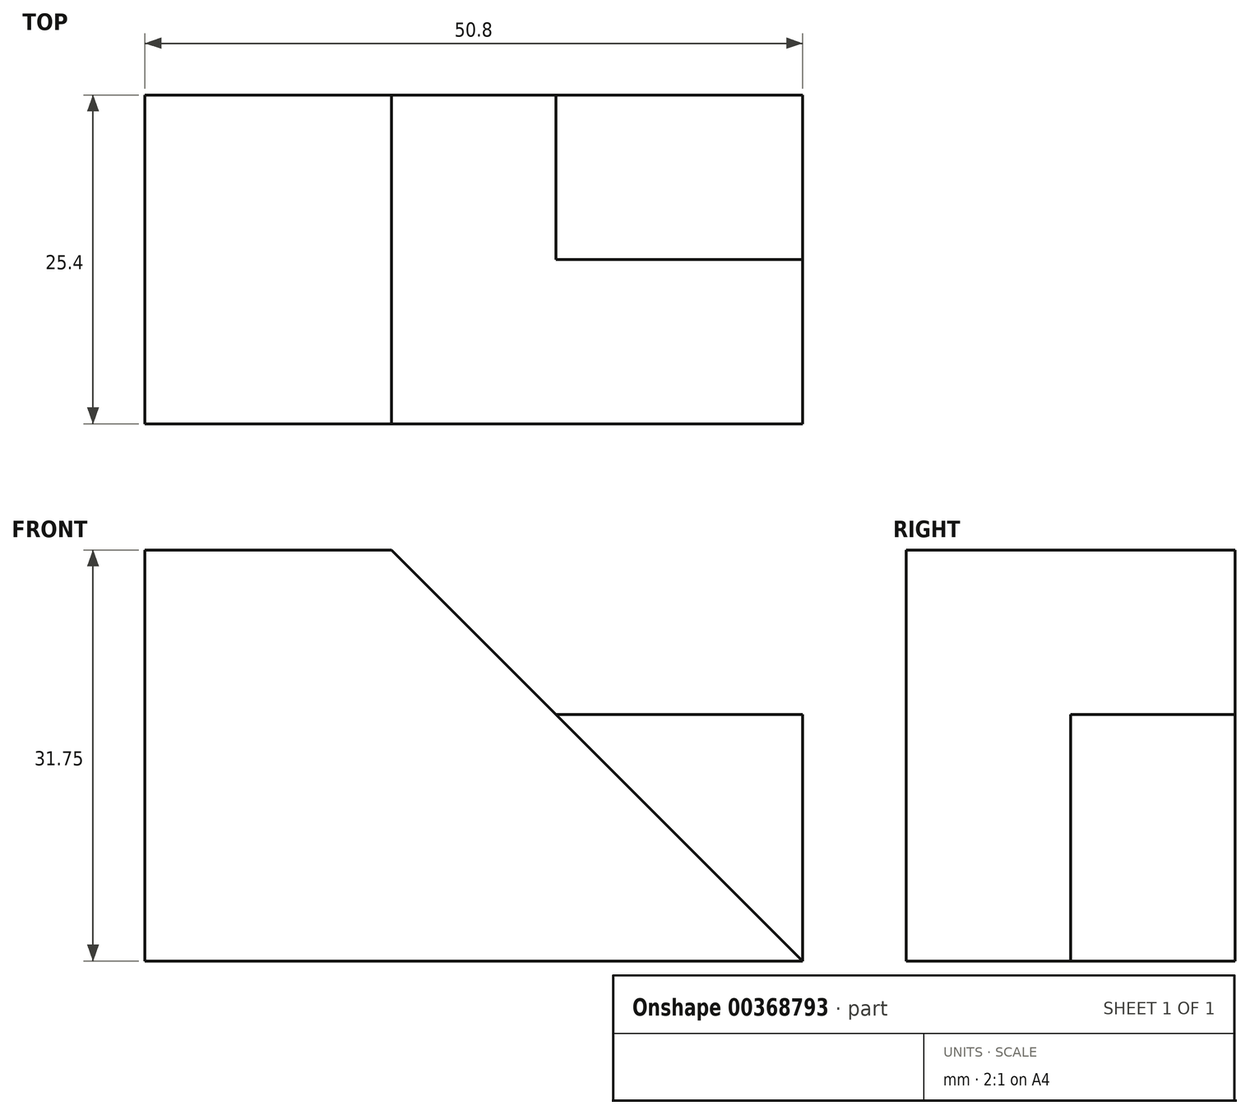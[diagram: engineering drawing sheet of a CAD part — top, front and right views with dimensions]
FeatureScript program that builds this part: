
annotation { "Feature Type Name" : "Feature", "Feature Type Description" : "" }
export const myFeature = defineFeature(function(context is Context, id is Id, definition is map)
    precondition{}
    {
        {
            var Q0;
            Q0=qCreatedBy(makeId("Front.planeOp"),FACE);
            var sketch = newSketch(context, id + "F0", { "sketchPlane" : qUnion([Q0])});
            skLineSegment(sketch, "E0.bottom", {"start": v(0, 31.75) * mm, "end": v(50.8, 31.75) * mm});
            skLineSegment(sketch, "E0.top", {"start": v(0, 0) * mm, "end": v(50.8, 0) * mm});
            skLineSegment(sketch, "E0.left", {"start": v(0, 31.75) * mm, "end": v(0, 0) * mm});
            skLineSegment(sketch, "E0.right", {"start": v(50.8, 31.75) * mm, "end": v(50.8, 0) * mm});
            skSolve(sketch);
        }
        {
            var Q0;
            Q0 = qSketchRegion(id + "FAowoq1lq1kOuDw_0", true);
            var Q1;
            Q1=makeQuery(id+"F0.imprint","IMPRINT",FACE,{"disambiguationData":[TD([[makeQuery(id+"F0.imprint","IMPRINT",EDGE,{"derivedFrom":sQuery(id+"F0.wireOp",EDGE,"E0.bottom")}),-1.0]])]});
            extrude(context, id + "F1", {"entities" : qUnion([Q0, Q1]), "depth" : 25.4 * mm});
        }
        {
            var Q0;
            Q0=makeQuery(id+"F1.opExtrude","CAP_FACE",FACE,{"disambiguationData":[OSD([sQuery(id+"F0.wireOp",EDGE,"E0.bottom"),sQuery(id+"F0.wireOp",EDGE,"E0.top"),sQuery(id+"F0.wireOp",EDGE,"E0.left"),sQuery(id+"F0.wireOp",EDGE,"E0.right")])],"isStart":false});
            var sketch = newSketch(context, id + "F2", { "sketchPlane" : qUnion([Q0])});
            skLineSegment(sketch, "E1", {"start": v(50.8, 0) * mm, "end": v(25.4, 31.75) * mm});
            skSolve(sketch);
        }
        {
            var Q0;
            {var subQ0=sQuery(id+"F2.wireOp",EDGE,"E1");Q0=makeQuery(id+"F2.imprint","IMPRINT",FACE,{"disambiguationData":[TD([[makeQuery(id+"F2.imprint","IMPRINT",EDGE,{"derivedFrom":subQ0}),-1.0]])]});}
            extrude(context, id + "F3", {"entities" : qUnion([Q0]), "operationType" : NewBodyOperationType.REMOVE, "oppositeDirection" : true, "depth" : 25.4 * mm});
        }
        {
            var Q0;
            Q0=makeQuery(id+"F3.boolean.opBoolean","COPY",FACE,{"derivedFrom":makeQuery(id+"F3.opExtrude","SWEPT_FACE",FACE,{"disambiguationData":[OSD([sQuery(id+"F2.wireOp",EDGE,"E1")])]})});
            extrude(context, id + "F4", {"entities" : qUnion([Q0]), "operationType" : NewBodyOperationType.ADD, "depth" : 25.4 * mm});
        }
        {
            var Q0;
            {var subQ0=sQuery(id+"F2.wireOp",EDGE,"E1");Q0=makeQuery(id+"F4.boolean.opBoolean","MERGE",FACE,{"derivedFrom":[makeQuery(id+"F1.opExtrude","CAP_FACE",FACE,{"disambiguationData":[OSD([sQuery(id+"F0.wireOp",EDGE,"E0.bottom"),sQuery(id+"F0.wireOp",EDGE,"E0.top"),sQuery(id+"F0.wireOp",EDGE,"E0.left"),sQuery(id+"F0.wireOp",EDGE,"E0.right")])],"isStart":false}),makeQuery(id+"F4.opExtrude","SWEPT_FACE",FACE,{"disambiguationData":[OSD([subQ0]),TDD([makeQuery(id+"F3.boolean.opBoolean","COPY",EDGE,{"derivedFrom":makeQuery(id+"F3.opExtrude","CAP_EDGE",EDGE,{"disambiguationData":[OSD([subQ0])],"isStart":true})})])]})]});}
            var sketch = newSketch(context, id + "F5", { "sketchPlane" : qUnion([Q0])});
            skLineSegment(sketch, "E2", {"start": v(25.4, 31.75) * mm, "end": v(50.8, 31.75) * mm});
            skLineSegment(sketch, "E3", {"start": v(50.8, 31.75) * mm, "end": v(50.8, 0) * mm});
            skSolve(sketch);
        }
        {
            var Q0;
            Q0=makeQuery(id+"F5.imprint","IMPRINT",FACE,{"disambiguationData":[TD([[makeQuery(id+"F5.imprint","IMPRINT",EDGE,{"derivedFrom":sQuery(id+"F5.wireOp",EDGE,"E2")}),1.0]])]});
            extrude(context, id + "F6", {"entities" : qUnion([Q0]), "operationType" : NewBodyOperationType.REMOVE, "oppositeDirection" : true, "depth" : 25.4 * mm});
        }
        {
            var Q0;
            {var subQ0=sQuery(id+"F2.wireOp",EDGE,"E1");Q0=makeQuery(id+"F4.boolean.opBoolean","MERGE",FACE,{"derivedFrom":[makeQuery(id+"F1.opExtrude","CAP_FACE",FACE,{"disambiguationData":[OSD([sQuery(id+"F0.wireOp",EDGE,"E0.bottom"),sQuery(id+"F0.wireOp",EDGE,"E0.top"),sQuery(id+"F0.wireOp",EDGE,"E0.left"),sQuery(id+"F0.wireOp",EDGE,"E0.right")])],"isStart":false}),makeQuery(id+"F4.opExtrude","SWEPT_FACE",FACE,{"disambiguationData":[OSD([subQ0]),TDD([makeQuery(id+"F3.boolean.opBoolean","COPY",EDGE,{"derivedFrom":makeQuery(id+"F3.opExtrude","CAP_EDGE",EDGE,{"disambiguationData":[OSD([subQ0])],"isStart":true})})])]})]});}
            var sketch = newSketch(context, id + "F7", { "sketchPlane" : qUnion([Q0])});
            skLineSegment(sketch, "E4", {"start": v(50.8, 0) * mm, "end": v(19.05, 31.75) * mm});
            skSolve(sketch);
        }
        {
            var Q0;
            {var subQ0=sQuery(id+"F7.wireOp",EDGE,"E4");Q0=makeQuery(id+"F7.imprint","IMPRINT",FACE,{"disambiguationData":[TD([[makeQuery(id+"F7.imprint","IMPRINT",EDGE,{"derivedFrom":subQ0}),-1.0]])]});}
            extrude(context, id + "F8", {"entities" : qUnion([Q0]), "operationType" : NewBodyOperationType.REMOVE, "oppositeDirection" : true, "depth" : 12.7 * mm});
        }
        {
            var Q0;
            Q0=makeQuery(id+"F8.boolean.opBoolean","COPY",FACE,{"derivedFrom":makeQuery(id+"F8.opExtrude","CAP_FACE",FACE,{"disambiguationData":[OSD([sQuery(id+"F0.wireOp",EDGE,"E0.bottom"),sQuery(id+"F5.wireOp",EDGE,"E2"),sQuery(id+"F5.wireOp",EDGE,"E3"),sQuery(id+"F7.wireOp",EDGE,"E4")])],"isStart":false})});
            var sketch = newSketch(context, id + "F9", { "sketchPlane" : qUnion([Q0])});
            skLineSegment(sketch, "E5", {"start": v(50.8, 19.05) * mm, "end": v(31.75, 19.05) * mm});
            skSolve(sketch);
        }
        {
            var Q0;
            {var subQ0=sQuery(id+"F9.wireOp",EDGE,"E5");Q0=makeQuery(id+"F9.imprint","IMPRINT",FACE,{"disambiguationData":[TD([[makeQuery(id+"F9.imprint","IMPRINT",EDGE,{"derivedFrom":subQ0}),-1.0]])]});}
            extrude(context, id + "F10", {"entities" : qUnion([Q0]), "operationType" : NewBodyOperationType.REMOVE, "oppositeDirection" : true, "depth" : 25.4 * mm});
        }
    });
